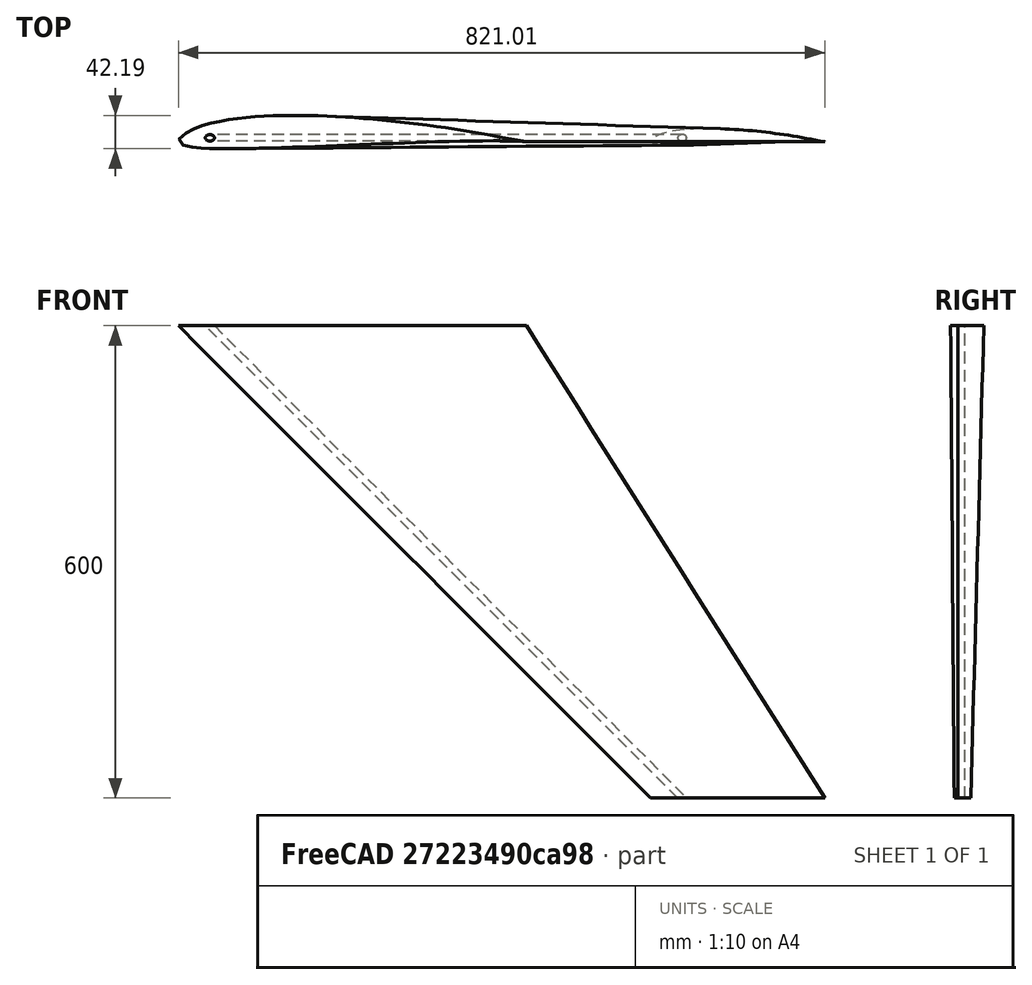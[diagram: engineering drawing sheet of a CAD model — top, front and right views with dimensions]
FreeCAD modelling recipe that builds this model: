
FCSTD DOCUMENT  (FreeCAD 1.0R39109 (Git))
Label: SD7037_vorlage
License: All rights reserved
LicenseURL: https://en.wikipedia.org/wiki/All_rights_reserved
objects: Part::Part2DObjectPython×3, Sketcher::SketchObject×3, App::DocumentObjectGroup×1, PartDesign::AdditiveLoft×1, PartDesign::Plane×1, PartDesign::Pocket×1, PartDesign::Body×1
note: 17 computed .brp shape members not serialized (recipe doc carries the construction recipe); baked Part::Feature solids carry a one-line shape summary decoded from their .brp

FEATURE [Part::Part2DObjectPython] Wire  # Draft 2D object (typed FeaturePython)
  Area = 0.0605284
  ChamferSize = 0
  Closed = true
  End = (1,0,0)
  FilletRadius = 0
  Length = 2.02979
  MakeFace = true
  Points = (61) [(1,0,0),(0.99672,0.00042,0),(0.98707,0.0018,0),(0.97146,0.00436,0),(0.95041,0.00811,0),(0.9245,0.01295,0),(0.89425,0.01865,0),(0.86015,0.0249,0),+53 more]
  Start = (1,0,0)
  Subdivisions = 0
FEATURE [App::DocumentObjectGroup] sd7037
  Group = -> [Wire]
FEATURE [Part::Part2DObjectPython] BSpline  label="wingtip"  # Draft 2D object (typed FeaturePython)
  Area = 2965.6
  Closed = true
  MakeFace = true
  Parameterization = 1
  Points = (60) [(221,0,0),(220.275,0.09282,0),(218.142,0.3978,0),(214.693,0.96356,0),(210.041,1.79231,0),(204.315,2.86195,0),(197.629,4.12165,0),(190.093,5.5029,0),+52 more]
FEATURE [Part::Part2DObjectPython] BSpline001  label="wingbase"  # Draft 2D object (typed FeaturePython)
  Area = 11862.4
  Closed = true
  MakeFace = true
  Parameterization = 1
  Points = (60) [(442,0,0),(440.55,0.18564,0),(436.285,0.7956,0),(429.385,1.92712,0),(420.081,3.58462,0),(408.629,5.7239,0),(395.258,8.2433,0),(380.186,11.0058,0),+52 more]
FEATURE [Sketcher::SketchObject] Sketch
  ArcFitTolerance = 1e-06
  FullyConstrained = false
  MakeInternals = false
  Placement = pos=(600,0,-600) rot=(0,0,1;0rad)
  sketch-geometry (123):
    g0: BSplineCurve PolesCount=61 KnotsCount=61 Degree=3 IsPeriodic=1
    g1-g61: Circle [constr] x61 (B-spline internal-alignment scaffolding for g0; pole/knot coordinates omitted)
    g62-g122: GeomPoint [constr] x61 (B-spline internal-alignment scaffolding for g0; pole/knot coordinates omitted)
  constraints (123):
    c: InternalAlignment(g1,g0)
    c: Weight(g1) = 1
    c: InternalAlignment(g2,g0)
    c: Equal(g2,g1)
    c: InternalAlignment(g3,g0)
    c: Equal(g3,g1)
    c: InternalAlignment(g4,g0)
    c: Equal(g4,g1)
    c: InternalAlignment(g5,g0)
    c: Equal(g5,g1)
    c: InternalAlignment(g6,g0)
    c: Equal(g6,g1)
    c: InternalAlignment(g7,g0)
    c: Equal(g7,g1)
    c: InternalAlignment(g8,g0)
    c: Equal(g8,g1)
    c: InternalAlignment(g9,g0)
    c: Equal(g9,g1)
    c: InternalAlignment(g10,g0)
    c: Equal(g10,g1)
    c: InternalAlignment(g11,g0)
    c: Equal(g11,g1)
    c: InternalAlignment(g12,g0)
    c: Equal(g12,g1)
    c: InternalAlignment(g13,g0)
    c: Equal(g13,g1)
    c: InternalAlignment(g14,g0)
    c: Equal(g14,g1)
    c: InternalAlignment(g15,g0)
    c: Equal(g15,g1)
    c: InternalAlignment(g16,g0)
    c: Equal(g16,g1)
    c: InternalAlignment(g17,g0)
    c: Equal(g17,g1)
    c: InternalAlignment(g18,g0)
    c: Equal(g18,g1)
    c: InternalAlignment(g19,g0)
    c: Equal(g19,g1)
    c: InternalAlignment(g20,g0)
    c: Equal(g20,g1)
    c: InternalAlignment(g21,g0)
    c: Equal(g21,g1)
    c: InternalAlignment(g22,g0)
    c: Equal(g22,g1)
    c: InternalAlignment(g23,g0)
    c: Equal(g23,g1)
    c: InternalAlignment(g24,g0)
    c: Equal(g24,g1)
    c: InternalAlignment(g25,g0)
    c: Equal(g25,g1)
    c: InternalAlignment(g26,g0)
    c: Equal(g26,g1)
    c: InternalAlignment(g27,g0)
    c: Equal(g27,g1)
    c: InternalAlignment(g28,g0)
    c: Equal(g28,g1)
    c: InternalAlignment(g29,g0)
    c: Equal(g29,g1)
    c: InternalAlignment(g30,g0)
    c: Equal(g30,g1)
    c: InternalAlignment(g31,g0)
    c: Equal(g31,g1)
    c: InternalAlignment(g32,g0)
    c: Equal(g32,g1)
    c: InternalAlignment(g33,g0)
    c: Equal(g33,g1)
    c: InternalAlignment(g34,g0)
    c: Equal(g34,g1)
    c: InternalAlignment(g35,g0)
    c: Equal(g35,g1)
    c: InternalAlignment(g36,g0)
    c: Equal(g36,g1)
    c: InternalAlignment(g37,g0)
    c: Equal(g37,g1)
    c: InternalAlignment(g38,g0)
    c: Equal(g38,g1)
    c: InternalAlignment(g39,g0)
    c: Equal(g39,g1)
    c: InternalAlignment(g40,g0)
    c: Equal(g40,g1)
    c: InternalAlignment(g41,g0)
    c: Equal(g41,g1)
    c: InternalAlignment(g42,g0)
    c: Equal(g42,g1)
    c: InternalAlignment(g43,g0)
    c: Equal(g43,g1)
    c: InternalAlignment(g44,g0)
    c: Equal(g44,g1)
    c: InternalAlignment(g45,g0)
    c: Equal(g45,g1)
    c: InternalAlignment(g46,g0)
    c: Equal(g46,g1)
    c: InternalAlignment(g47,g0)
    c: Equal(g47,g1)
    c: InternalAlignment(g48,g0)
    c: Equal(g48,g1)
    c: InternalAlignment(g49,g0)
    c: Equal(g49,g1)
    c: InternalAlignment(g50,g0)
    c: Equal(g50,g1)
    c: InternalAlignment(g51,g0)
    c: Equal(g51,g1)
    c: InternalAlignment(g52,g0)
    c: Equal(g52,g1)
    c: InternalAlignment(g53,g0)
    c: Equal(g53,g1)
    c: InternalAlignment(g54,g0)
    c: Equal(g54,g1)
    c: InternalAlignment(g55,g0)
    c: Equal(g55,g1)
    c: InternalAlignment(g56,g0)
    c: Equal(g56,g1)
    c: InternalAlignment(g57,g0)
    c: Equal(g57,g1)
    c: InternalAlignment(g58,g0)
    c: Equal(g58,g1)
    c: InternalAlignment(g59,g0)
    c: Equal(g59,g1)
    c: InternalAlignment(g60,g0)
    c: Equal(g60,g1)
    c: InternalAlignment(g61,g0)
    c: Equal(g61,g1)
    c: InternalAlignment(g62-g122 -> g0) x61
FEATURE [Sketcher::SketchObject] Sketch001
  ArcFitTolerance = 1e-06
  FullyConstrained = false
  MakeInternals = false
  sketch-geometry (123):
    g0: BSplineCurve PolesCount=61 KnotsCount=61 Degree=3 IsPeriodic=1
    g1-g61: Circle [constr] x61 (B-spline internal-alignment scaffolding for g0; pole/knot coordinates omitted)
    g62-g122: GeomPoint [constr] x61 (B-spline internal-alignment scaffolding for g0; pole/knot coordinates omitted)
  constraints (123):
    c: InternalAlignment(g1,g0)
    c: Weight(g1) = 1
    c: InternalAlignment(g2,g0)
    c: Equal(g2,g1)
    c: InternalAlignment(g3,g0)
    c: Equal(g3,g1)
    c: InternalAlignment(g4,g0)
    c: Equal(g4,g1)
    c: InternalAlignment(g5,g0)
    c: Equal(g5,g1)
    c: InternalAlignment(g6,g0)
    c: Equal(g6,g1)
    c: InternalAlignment(g7,g0)
    c: Equal(g7,g1)
    c: InternalAlignment(g8,g0)
    c: Equal(g8,g1)
    c: InternalAlignment(g9,g0)
    c: Equal(g9,g1)
    c: InternalAlignment(g10,g0)
    c: Equal(g10,g1)
    c: InternalAlignment(g11,g0)
    c: Equal(g11,g1)
    c: InternalAlignment(g12,g0)
    c: Equal(g12,g1)
    c: InternalAlignment(g13,g0)
    c: Equal(g13,g1)
    c: InternalAlignment(g14,g0)
    c: Equal(g14,g1)
    c: InternalAlignment(g15,g0)
    c: Equal(g15,g1)
    c: InternalAlignment(g16,g0)
    c: Equal(g16,g1)
    c: InternalAlignment(g17,g0)
    c: Equal(g17,g1)
    c: InternalAlignment(g18,g0)
    c: Equal(g18,g1)
    c: InternalAlignment(g19,g0)
    c: Equal(g19,g1)
    c: InternalAlignment(g20,g0)
    c: Equal(g20,g1)
    c: InternalAlignment(g21,g0)
    c: Equal(g21,g1)
    c: InternalAlignment(g22,g0)
    c: Equal(g22,g1)
    c: InternalAlignment(g23,g0)
    c: Equal(g23,g1)
    c: InternalAlignment(g24,g0)
    c: Equal(g24,g1)
    c: InternalAlignment(g25,g0)
    c: Equal(g25,g1)
    c: InternalAlignment(g26,g0)
    c: Equal(g26,g1)
    c: InternalAlignment(g27,g0)
    c: Equal(g27,g1)
    c: InternalAlignment(g28,g0)
    c: Equal(g28,g1)
    c: InternalAlignment(g29,g0)
    c: Equal(g29,g1)
    c: InternalAlignment(g30,g0)
    c: Equal(g30,g1)
    c: InternalAlignment(g31,g0)
    c: Equal(g31,g1)
    c: InternalAlignment(g32,g0)
    c: Equal(g32,g1)
    c: InternalAlignment(g33,g0)
    c: Equal(g33,g1)
    c: InternalAlignment(g34,g0)
    c: Equal(g34,g1)
    c: InternalAlignment(g35,g0)
    c: Equal(g35,g1)
    c: InternalAlignment(g36,g0)
    c: Equal(g36,g1)
    c: InternalAlignment(g37,g0)
    c: Equal(g37,g1)
    c: InternalAlignment(g38,g0)
    c: Equal(g38,g1)
    c: InternalAlignment(g39,g0)
    c: Equal(g39,g1)
    c: InternalAlignment(g40,g0)
    c: Equal(g40,g1)
    c: InternalAlignment(g41,g0)
    c: Equal(g41,g1)
    c: InternalAlignment(g42,g0)
    c: Equal(g42,g1)
    c: InternalAlignment(g43,g0)
    c: Equal(g43,g1)
    c: InternalAlignment(g44,g0)
    c: Equal(g44,g1)
    c: InternalAlignment(g45,g0)
    c: Equal(g45,g1)
    c: InternalAlignment(g46,g0)
    c: Equal(g46,g1)
    c: InternalAlignment(g47,g0)
    c: Equal(g47,g1)
    c: InternalAlignment(g48,g0)
    c: Equal(g48,g1)
    c: InternalAlignment(g49,g0)
    c: Equal(g49,g1)
    c: InternalAlignment(g50,g0)
    c: Equal(g50,g1)
    c: InternalAlignment(g51,g0)
    c: Equal(g51,g1)
    c: InternalAlignment(g52,g0)
    c: Equal(g52,g1)
    c: InternalAlignment(g53,g0)
    c: Equal(g53,g1)
    c: InternalAlignment(g54,g0)
    c: Equal(g54,g1)
    c: InternalAlignment(g55,g0)
    c: Equal(g55,g1)
    c: InternalAlignment(g56,g0)
    c: Equal(g56,g1)
    c: InternalAlignment(g57,g0)
    c: Equal(g57,g1)
    c: InternalAlignment(g58,g0)
    c: Equal(g58,g1)
    c: InternalAlignment(g59,g0)
    c: Equal(g59,g1)
    c: InternalAlignment(g60,g0)
    c: Equal(g60,g1)
    c: InternalAlignment(g61,g0)
    c: Equal(g61,g1)
    c: InternalAlignment(g62-g122 -> g0) x61
FEATURE [PartDesign::AdditiveLoft] AdditiveLoft
  Closed = false
  Profile = -> Sketch001
  Refine = true
  Ruled = false
  Sections = -> [Sketch]
  Suppressed = false
FEATURE [PartDesign::Plane] DatumPlane
  AttachmentOffset = pos=(0,0,0) rot=(0,-1,0;0.785398rad)
  AttachmentSupport = -> [AdditiveLoft]
  Length = 82.6027
  MapMode = 5
  Placement = pos=(0,0,0) rot=(0,-1,0;0.785398rad)
  ResizeMode = 0
  Width = 61.8921
FEATURE [Sketcher::SketchObject] Sketch002
  ArcFitTolerance = 1e-06
  AttachmentSupport = -> [DatumPlane]
  FullyConstrained = false
  MakeInternals = false
  MapMode = 5
  Placement = pos=(0,0,0) rot=(0,-1,0;0.785398rad)
  sketch-geometry (1):
    g0: Circle CenterX=28.3343 CenterY=4.75298 CenterZ=0 NormalX=0 NormalY=0 NormalZ=1 AngleXU=0 Radius=4.1
  constraints (1):
    c: Diameter(g0) = 8.2
FEATURE [PartDesign::Pocket] Pocket
  BaseFeature = -> AdditiveLoft
  Direction = (0.707107,0,-0.707107)
  Length = 1000
  Length2 = 5
  Profile = -> Sketch002
  ReferenceAxis = -> Sketch002 [N_Axis]
  Refine = true
  Suppressed = false
  Type = 0
FEATURE [PartDesign::Body] Body
  AllowCompound = false
  Group = -> [Sketch001,Sketch,AdditiveLoft,DatumPlane,Sketch002,Pocket]
  Origin = -> Origin
  Tip = -> Pocket
